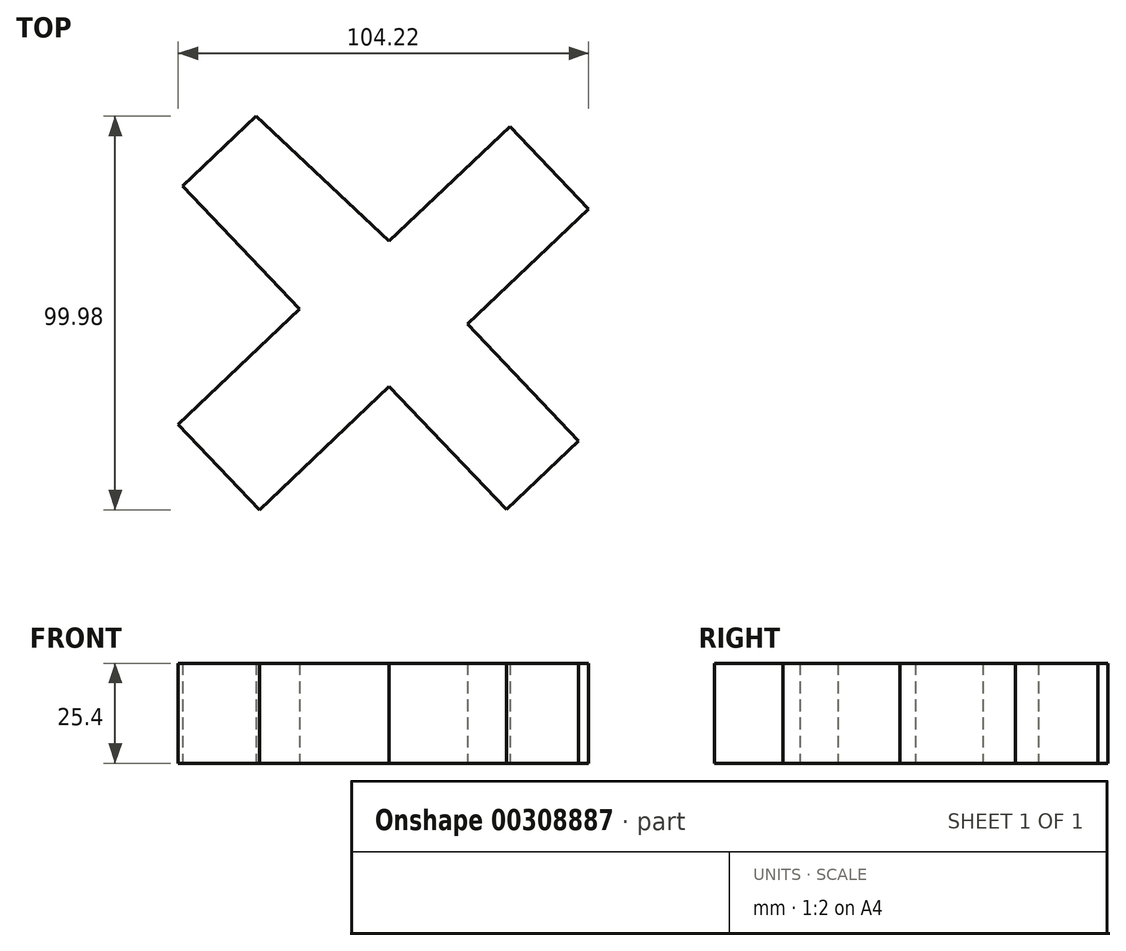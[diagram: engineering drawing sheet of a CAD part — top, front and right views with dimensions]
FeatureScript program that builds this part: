
annotation { "Feature Type Name" : "Feature", "Feature Type Description" : "" }
export const myFeature = defineFeature(function(context is Context, id is Id, definition is map)
    precondition{}
    {
        {
            var Q0;
            Q0=qCreatedBy(makeId("Top.planeOp"),FACE);
            var sketch = newSketch(context, id + "F0", { "sketchPlane" : qUnion([Q0])});
            skLineSegment(sketch, "E0", {"start": v(-33.83, 37.03) * mm, "end": v(-52.43, 19.35) * mm});
            skLineSegment(sketch, "E1", {"start": v(-52.43, 19.35) * mm, "end": v(-22.7, -11.91) * mm});
            skLineSegment(sketch, "E2", {"start": v(-22.7, -11.91) * mm, "end": v(-53.58, -41.28) * mm});
            skLineSegment(sketch, "E3", {"start": v(-53.58, -41.28) * mm, "end": v(-32.97, -62.95) * mm});
            skLineSegment(sketch, "E4", {"start": v(-32.97, -62.95) * mm, "end": v(0, -31.6) * mm});
            skLineSegment(sketch, "E5", {"start": v(0, -31.6) * mm, "end": v(29.8, -62.93) * mm});
            skLineSegment(sketch, "E6", {"start": v(29.8, -62.93) * mm, "end": v(48.13, -45.49) * mm});
            skLineSegment(sketch, "E7", {"start": v(48.13, -45.49) * mm, "end": v(19.87, -15.76) * mm});
            skLineSegment(sketch, "E8", {"start": v(19.87, -15.76) * mm, "end": v(50.64, 13.5) * mm});
            skLineSegment(sketch, "E9", {"start": v(50.64, 13.5) * mm, "end": v(30.7, 34.47) * mm});
            skLineSegment(sketch, "E10", {"start": v(30.7, 34.47) * mm, "end": v(0, 5.28) * mm});
            skLineSegment(sketch, "E11", {"start": v(0, 5.28) * mm, "end": v(-33.83, 37.03) * mm});
            skSolve(sketch);
        }
        {
            var Q0;
            Q0=makeQuery(id+"F0.imprint","IMPRINT",FACE,{"disambiguationData":[TD([[makeQuery(id+"F0.imprint","IMPRINT",EDGE,{"derivedFrom":sQuery(id+"F0.wireOp",EDGE,"E0")}),1.0]])]});
            extrude(context, id + "F1", {"entities" : qUnion([Q0]), "depth" : 25.4 * mm});
        }
    });
